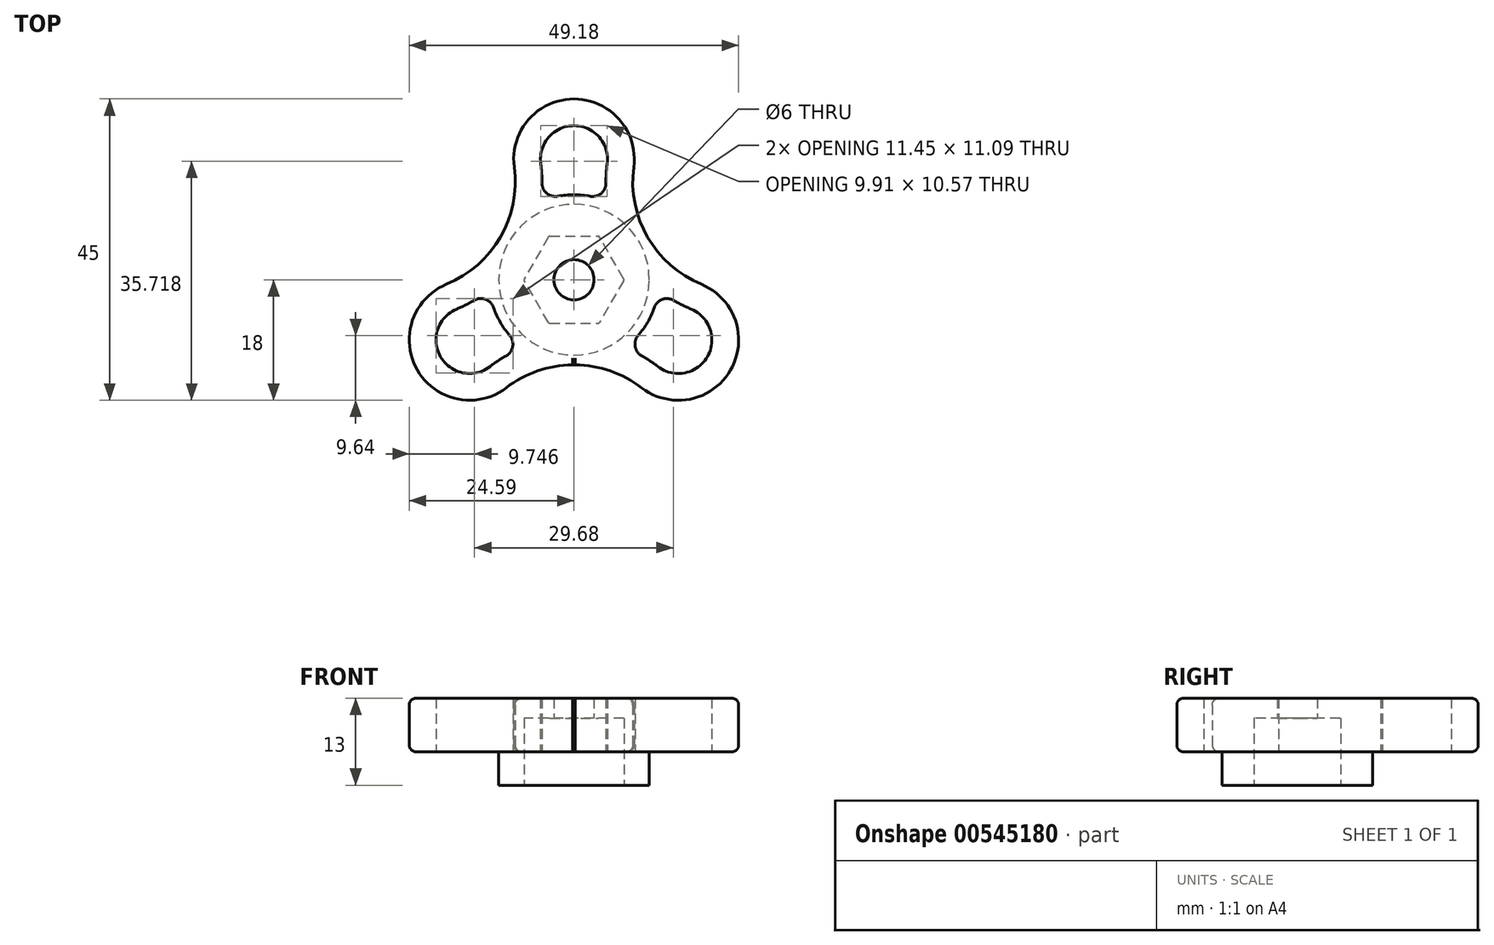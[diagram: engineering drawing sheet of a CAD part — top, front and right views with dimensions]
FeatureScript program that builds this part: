
annotation { "Feature Type Name" : "Feature", "Feature Type Description" : "" }
export const myFeature = defineFeature(function(context is Context, id is Id, definition is map)
    precondition{}
    {
        {
            var Q0;
            Q0=qCreatedBy(makeId("Top.planeOp"),FACE);
            var sketch = newSketch(context, id + "F0", { "sketchPlane" : qUnion([Q0])});
            skCircle(sketch, "E0", {"center": v(0, 0) * mm, "radius": 3 * mm});
            skLineSegment(sketch, "E1", {"start": v(0, 27) * mm, "end": v(0, 18) * mm, "construction": true});
            skArc(sketch, "E2", {"start": v(8.92, 16.82) * mm, "mid": v(0, 27) * mm, "end": v(-8.92, 16.82) * mm});
            skArc(sketch, "E3.1.0", {"start": v(-19.03, -0.68) * mm, "mid": v(-23.39, -13.5) * mm, "end": v(-10.11, -16.14) * mm});
            skArc(sketch, "E3.2.0", {"start": v(10.1, -16.14) * mm, "mid": v(23.38, -13.5) * mm, "end": v(19.02, -0.69) * mm});
            skLineSegment(sketch, "E4.trimOffspring", {"start": v(11, 6.35) * mm, "end": v(11, 6.35) * mm});
            skArc(sketch, "E5.trimOffspring", {"start": v(-0.21, -12.7) * mm, "mid": v(0, -12.7) * mm, "end": v(0.2, -12.7) * mm});
            skArc(sketch, "E6", {"start": v(8.92, 16.82) * mm, "mid": v(11, 6.35) * mm, "end": v(19.02, -0.69) * mm});
            skPoint(sketch, "E6.first.point", {"position": v(19.02, -0.69) * mm});
            skPoint(sketch, "E6.second.point", {"position": v(11, 6.35) * mm});
            skPoint(sketch, "E6.third.point", {"position": v(8.92, 16.82) * mm});
            skArc(sketch, "E7.1.0", {"start": v(-19.03, -0.68) * mm, "mid": v(-11, 6.35) * mm, "end": v(-8.92, 16.82) * mm});
            skArc(sketch, "E7.2.0", {"start": v(10.1, -16.14) * mm, "mid": v(0, -12.7) * mm, "end": v(-10.11, -16.14) * mm});
            skArc(sketch, "E8", {"start": v(2.4, 12.47) * mm, "mid": v(0, 12.7) * mm, "end": v(-2.4, 12.47) * mm});
            skArc(sketch, "E9.0", {"start": v(4.96, 17.34) * mm, "mid": v(0, 23) * mm, "end": v(-4.96, 17.35) * mm});
            skArc(sketch, "E10.0", {"start": v(-17.5, -4.38) * mm, "mid": v(-16.18, -3.78) * mm, "end": v(-14.9, -3.09) * mm});
            skArc(sketch, "E11.0", {"start": v(4.96, 17.34) * mm, "mid": v(4.82, 15.9) * mm, "end": v(4.78, 14.45) * mm});
            skArc(sketch, "E12.0", {"start": v(12.54, -12.97) * mm, "mid": v(11.36, -12.13) * mm, "end": v(10.12, -11.37) * mm});
            skArc(sketch, "E13.0", {"start": v(12.54, -12.97) * mm, "mid": v(19.92, -11.5) * mm, "end": v(17.5, -4.38) * mm});
            skArc(sketch, "E14.0", {"start": v(-17.5, -4.38) * mm, "mid": v(-19.93, -11.5) * mm, "end": v(-12.55, -12.96) * mm});
            skArc(sketch, "E15.trimOffspring", {"start": v(14.9, -3.1) * mm, "mid": v(16.18, -3.78) * mm, "end": v(17.5, -4.38) * mm});
            skArc(sketch, "E16.trimOffspring", {"start": v(-10.13, -11.36) * mm, "mid": v(-11.37, -12.12) * mm, "end": v(-12.55, -12.96) * mm});
            skArc(sketch, "E17.trimOffspring", {"start": v(9.6, -8.32) * mm, "mid": v(11, -6.35) * mm, "end": v(12, -4.16) * mm});
            skArc(sketch, "E18.trimOffspring", {"start": v(-4.78, 14.45) * mm, "mid": v(-4.82, 15.9) * mm, "end": v(-4.96, 17.35) * mm});
            skArc(sketch, "E19.trimOffspring", {"start": v(-12, -4.15) * mm, "mid": v(-11, -6.35) * mm, "end": v(-9.6, -8.31) * mm});
            skPoint(sketch, "E20.visualSharp", {"position": v(5, 11.68) * mm});
            skArc(sketch, "E20.filletArc", {"start": v(2.4, 12.47) * mm, "mid": v(4.06, 12.9) * mm, "end": v(4.78, 14.45) * mm});
            skPoint(sketch, "E21.visualSharp", {"position": v(-5, 11.68) * mm});
            skArc(sketch, "E21.filletArc", {"start": v(-4.78, 14.45) * mm, "mid": v(-4.06, 12.9) * mm, "end": v(-2.4, 12.47) * mm});
            skPoint(sketch, "E22.visualSharp", {"position": v(12.6, -1.52) * mm});
            skArc(sketch, "E22.filletArc", {"start": v(14.9, -3.1) * mm, "mid": v(13.2, -2.94) * mm, "end": v(12, -4.16) * mm});
            skPoint(sketch, "E23.visualSharp", {"position": v(7.61, -10.16) * mm});
            skArc(sketch, "E23.filletArc", {"start": v(9.6, -8.32) * mm, "mid": v(9.14, -9.97) * mm, "end": v(10.12, -11.37) * mm});
            skPoint(sketch, "E24.visualSharp", {"position": v(-7.62, -10.16) * mm});
            skArc(sketch, "E24.filletArc", {"start": v(-10.13, -11.36) * mm, "mid": v(-9.14, -9.96) * mm, "end": v(-9.6, -8.31) * mm});
            skPoint(sketch, "E25.visualSharp", {"position": v(-12.61, -1.51) * mm});
            skArc(sketch, "E25.filletArc", {"start": v(-12, -4.15) * mm, "mid": v(-13.2, -2.93) * mm, "end": v(-14.9, -3.09) * mm});
            skSolve(sketch);
        }
        {
            var Q0;
            {var subQ0=sQuery(id+"F0.wireOp",EDGE,"E5.trimOffspring");Q0=makeQuery(id+"F0.imprint","IMPRINT",FACE,{"disambiguationData":[TD([[makeQuery(id+"F0.imprint","IMPRINT",EDGE,{"derivedFrom":subQ0}),1.0]])]});}
            var Q1;
            Q1=makeQuery(id+"F0.imprint","IMPRINT",FACE,{"disambiguationData":[TD([[makeQuery(id+"F0.imprint","IMPRINT",EDGE,{"derivedFrom":sQuery(id+"F0.wireOp",EDGE,"E0")}),-1.0]])]});
            extrude(context, id + "F1", {"entities" : qUnion([Q0, Q1]), "depth" : 8 * mm, "offsetDistance" : 25 * mm});
        }
        {
            var Q0;
            Q0=makeQuery(id+"F1.opExtrude","CAP_FACE",FACE,{"disambiguationData":[OSD([sQuery(id+"F0.wireOp",EDGE,"E0"),sQuery(id+"F0.wireOp",EDGE,"E2"),sQuery(id+"F0.wireOp",EDGE,"E3.1.0"),sQuery(id+"F0.wireOp",EDGE,"E3.2.0"),sQuery(id+"F0.wireOp",EDGE,"E5.trimOffspring"),sQuery(id+"F0.wireOp",EDGE,"E6"),sQuery(id+"F0.wireOp",EDGE,"E7.1.0"),sQuery(id+"F0.wireOp",EDGE,"E7.2.0"),sQuery(id+"F0.wireOp",EDGE,"E8"),sQuery(id+"F0.wireOp",EDGE,"E9.0"),sQuery(id+"F0.wireOp",EDGE,"E10.0"),sQuery(id+"F0.wireOp",EDGE,"E11.0"),sQuery(id+"F0.wireOp",EDGE,"E12.0"),sQuery(id+"F0.wireOp",EDGE,"E13.0"),sQuery(id+"F0.wireOp",EDGE,"E14.0"),sQuery(id+"F0.wireOp",EDGE,"E15.trimOffspring"),sQuery(id+"F0.wireOp",EDGE,"E16.trimOffspring"),sQuery(id+"F0.wireOp",EDGE,"E17.trimOffspring"),sQuery(id+"F0.wireOp",EDGE,"E18.trimOffspring"),sQuery(id+"F0.wireOp",EDGE,"E19.trimOffspring"),sQuery(id+"F0.wireOp",EDGE,"E20.filletArc"),sQuery(id+"F0.wireOp",EDGE,"E21.filletArc"),sQuery(id+"F0.wireOp",EDGE,"E22.filletArc"),sQuery(id+"F0.wireOp",EDGE,"E23.filletArc"),sQuery(id+"F0.wireOp",EDGE,"E24.filletArc"),sQuery(id+"F0.wireOp",EDGE,"E25.filletArc")])],"isStart":true});
            var sketch = newSketch(context, id + "F2", { "sketchPlane" : qUnion([Q0])});
            skCircle(sketch, "E26", {"center": v(0, 0) * mm, "radius": 11.25 * mm});
            skSolve(sketch);
        }
        {
            var Q0;
            Q0=makeQuery(id+"F2.imprint","IMPRINT",FACE,{"disambiguationData":[TD([[makeQuery(id+"F2.imprint","IMPRINT",EDGE,{"derivedFrom":sQuery(id+"F2.wireOp",EDGE,"E26")}),1.0]])]});
            extrude(context, id + "F3", {"entities" : qUnion([Q0]), "operationType" : NewBodyOperationType.ADD, "depth" : 5 * mm, "offsetDistance" : 25 * mm});
        }
        {
            var Q0;
            Q0=makeQuery(id+"F3.opExtrude","CAP_FACE",FACE,{"disambiguationData":[OSD([sQuery(id+"F0.wireOp",EDGE,"E0"),sQuery(id+"F2.wireOp",EDGE,"E26")])],"isStart":false});
            var sketch = newSketch(context, id + "F4", { "sketchPlane" : qUnion([Q0])});
            skLineSegment(sketch, "E27", {"start": v(-3.6, 6.5) * mm, "end": v(3.6, 6.5) * mm});
            skLineSegment(sketch, "E28.0", {"start": v(-3.6, -6.5) * mm, "end": v(3.6, -6.5) * mm});
            skLineSegment(sketch, "E29.1.0", {"start": v(-3.82, -6.38) * mm, "end": v(-7.43, -0.12) * mm});
            skLineSegment(sketch, "E29.1.1", {"start": v(7.43, 0.12) * mm, "end": v(3.82, 6.38) * mm});
            skLineSegment(sketch, "E29.2.0", {"start": v(7.43, -0.13) * mm, "end": v(3.82, -6.38) * mm});
            skLineSegment(sketch, "E29.2.1", {"start": v(-3.82, 6.38) * mm, "end": v(-7.43, 0.13) * mm});
            skCircle(sketch, "E30", {"center": v(0, 0) * mm, "radius": 3 * mm});
            skPoint(sketch, "E31.newPointB", {"position": v(3.75, 6.5) * mm});
            skArc(sketch, "E31.filletArc", {"start": v(3.82, 6.37) * mm, "mid": v(3.73, 6.47) * mm, "end": v(3.6, 6.5) * mm});
            skPoint(sketch, "E32.newPointA", {"position": v(-3.75, 6.5) * mm});
            skArc(sketch, "E32.filletArc", {"start": v(-3.6, 6.5) * mm, "mid": v(-3.73, 6.47) * mm, "end": v(-3.82, 6.38) * mm});
            skArc(sketch, "E33.filletArc", {"start": v(-7.43, 0.13) * mm, "mid": v(-7.47, 0) * mm, "end": v(-7.43, -0.12) * mm});
            skPoint(sketch, "E34.newPointA", {"position": v(7.5, 0) * mm});
            skArc(sketch, "E34.filletArc", {"start": v(7.43, -0.13) * mm, "mid": v(7.47, 0) * mm, "end": v(7.43, 0.12) * mm});
            skArc(sketch, "E35.filletArc", {"start": v(3.6, -6.5) * mm, "mid": v(3.73, -6.47) * mm, "end": v(3.82, -6.38) * mm});
            skArc(sketch, "E36.filletArc", {"start": v(-3.82, -6.38) * mm, "mid": v(-3.73, -6.47) * mm, "end": v(-3.6, -6.5) * mm});
            skSolve(sketch);
        }
        {
            var Q0;
            Q0=makeQuery(id+"F4.imprint","IMPRINT",FACE,{"disambiguationData":[TD([[makeQuery(id+"F4.imprint","IMPRINT",EDGE,{"derivedFrom":sQuery(id+"F4.wireOp",EDGE,"E27")}),-1.0]])]});
            extrude(context, id + "F5", {"entities" : qUnion([Q0]), "operationType" : NewBodyOperationType.REMOVE, "oppositeDirection" : true, "depth" : 10 * mm, "offsetDistance" : 25 * mm});
        }
        {
            var Q0;
            Q0=makeQuery(id+"F1.opExtrude","CAP_EDGE",EDGE,{"disambiguationData":[OSD([sQuery(id+"F0.wireOp",EDGE,"E2")])],"isStart":false});
            var Q1;
            Q1=makeQuery(id+"F3.opExtrude","CAP_EDGE",EDGE,{"disambiguationData":[OSD([sQuery(id+"F2.wireOp",EDGE,"E26")])],"isStart":true});
            fillet(context, id + "F6", {"entities" : qUnion([Q0, Q1]), "radius" : 1 * mm, "tangentPropagation" : true, "allowEdgeOverflow" : false});
        }
        {
            var Q0;
            Q0=makeQuery(id+"F1.opExtrude","CAP_EDGE",EDGE,{"disambiguationData":[OSD([sQuery(id+"F0.wireOp",EDGE,"E5.trimOffspring")])],"isStart":false});
            fillet(context, id + "F7", {"entities" : qUnion([Q0]), "radius" : 1 * mm, "tangentPropagation" : true, "allowEdgeOverflow" : false});
        }
        {
            var Q0;
            Q0=makeQuery(id+"F1.opExtrude","CAP_EDGE",EDGE,{"disambiguationData":[OSD([sQuery(id+"F0.wireOp",EDGE,"E3.1.0")])],"isStart":true});
            var Q1;
            {var subQ0=sQuery(id+"F0.wireOp",EDGE,"E7.2.0");Q1=makeQuery(id+"F1.opExtrude","CAP_EDGE",EDGE,{"disambiguationData":[OSD([subQ0]),TDD([makeQuery(id+"F0.imprint","IMPRINT",EDGE,{"disambiguationData":[TD([[makeQuery(id+"F0.imprint","INTERSECT",VERTEX,{"derivedFrom":[sQuery(id+"F0.wireOp",EDGE,"E3.1.0"),subQ0]}),1.0]])],"derivedFrom":subQ0})])],"isStart":true});}
            var Q2;
            {var subQ0=sQuery(id+"F0.wireOp",EDGE,"E7.2.0");Q2=makeQuery(id+"F1.opExtrude","CAP_EDGE",EDGE,{"disambiguationData":[OSD([subQ0]),TDD([makeQuery(id+"F0.imprint","IMPRINT",EDGE,{"disambiguationData":[TD([[makeQuery(id+"F0.imprint","INTERSECT",VERTEX,{"derivedFrom":[sQuery(id+"F0.wireOp",EDGE,"E3.2.0"),subQ0]}),-1.0]])],"derivedFrom":subQ0})])],"isStart":true});}
            var Q3;
            Q3=makeQuery(id+"F1.opExtrude","CAP_EDGE",EDGE,{"disambiguationData":[OSD([sQuery(id+"F0.wireOp",EDGE,"E5.trimOffspring")])],"isStart":true});
            fillet(context, id + "F8", {"entities" : qUnion([Q0, Q1, Q2, Q3]), "radius" : 1 * mm, "tangentPropagation" : true, "allowEdgeOverflow" : false});
        }
    });
